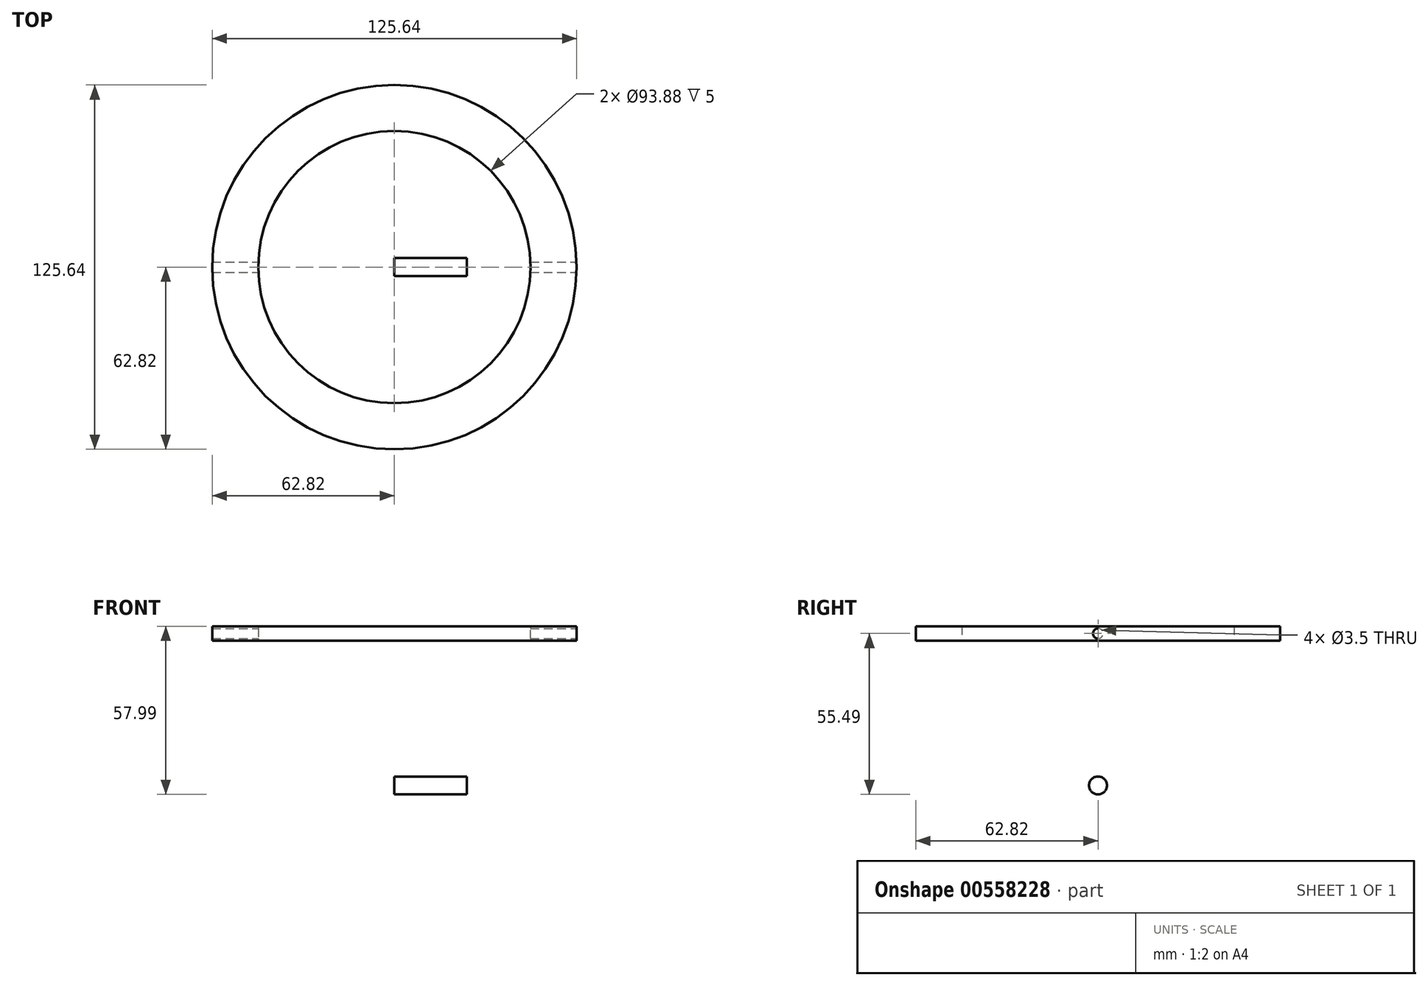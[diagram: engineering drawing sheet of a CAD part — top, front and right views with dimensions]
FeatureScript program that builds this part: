
annotation { "Feature Type Name" : "Feature", "Feature Type Description" : "" }
export const myFeature = defineFeature(function(context is Context, id is Id, definition is map)
    precondition{}
    {
        {
            var Q0;
            Q0=qCreatedBy(makeId("Top.planeOp"),FACE);
            var sketch = newSketch(context, id + "F0", { "sketchPlane" : qUnion([Q0])});
            skCircle(sketch, "E0", {"center": v(0, 0) * mm, "radius": 62.82 * mm});
            skCircle(sketch, "E1", {"center": v(0, 0) * mm, "radius": 46.94 * mm});
            skSolve(sketch);
        }
        {
            var Q0;
            Q0=makeQuery(id+"F0.imprint","IMPRINT",FACE,{"disambiguationData":[TD([[makeQuery(id+"F0.imprint","IMPRINT",EDGE,{"derivedFrom":sQuery(id+"F0.wireOp",EDGE,"E0")}),1.0]])]});
            extrude(context, id + "F1", {"entities" : qUnion([Q0]), "depth" : 5 * mm, "offsetDistance" : 25 * mm});
        }
        {
            var Q0;
            Q0=qCreatedBy(makeId("Right.planeOp"),FACE);
            var sketch = newSketch(context, id + "F2", { "sketchPlane" : qUnion([Q0])});
            skCircle(sketch, "E2", {"center": v(0, -49.89) * mm, "radius": 3.1 * mm});
            skSolve(sketch);
        }
        {
            var Q0;
            Q0=makeQuery(id+"F2.imprint","IMPRINT",FACE,{"disambiguationData":[TD([[makeQuery(id+"F2.imprint","IMPRINT",EDGE,{"derivedFrom":sQuery(id+"F2.wireOp",EDGE,"E2")}),1.0]])]});
            extrude(context, id + "F3", {"entities" : qUnion([Q0]), "depth" : 25 * mm, "offsetDistance" : 25 * mm});
        }
        {
            var Q0;
            Q0=qCreatedBy(makeId("Right.planeOp"),FACE);
            var sketch = newSketch(context, id + "F4", { "sketchPlane" : qUnion([Q0])});
            skCircle(sketch, "E3", {"center": v(0, 2.5) * mm, "radius": 1.75 * mm});
            skSolve(sketch);
        }
        {
            var Q0;
            Q0 = qSketchRegion(id + "F4", true);
            extrude(context, id + "F5", {"entities" : qUnion([Q0]), "operationType" : NewBodyOperationType.REMOVE, "oppositeDirection" : true, "depth" : 94.8 * mm, "offsetDistance" : 25 * mm, "hasSecondDirection" : true, "secondDirectionOppositeDirection" : false, "secondDirectionDepth" : 86.7 * mm});
        }
    });
